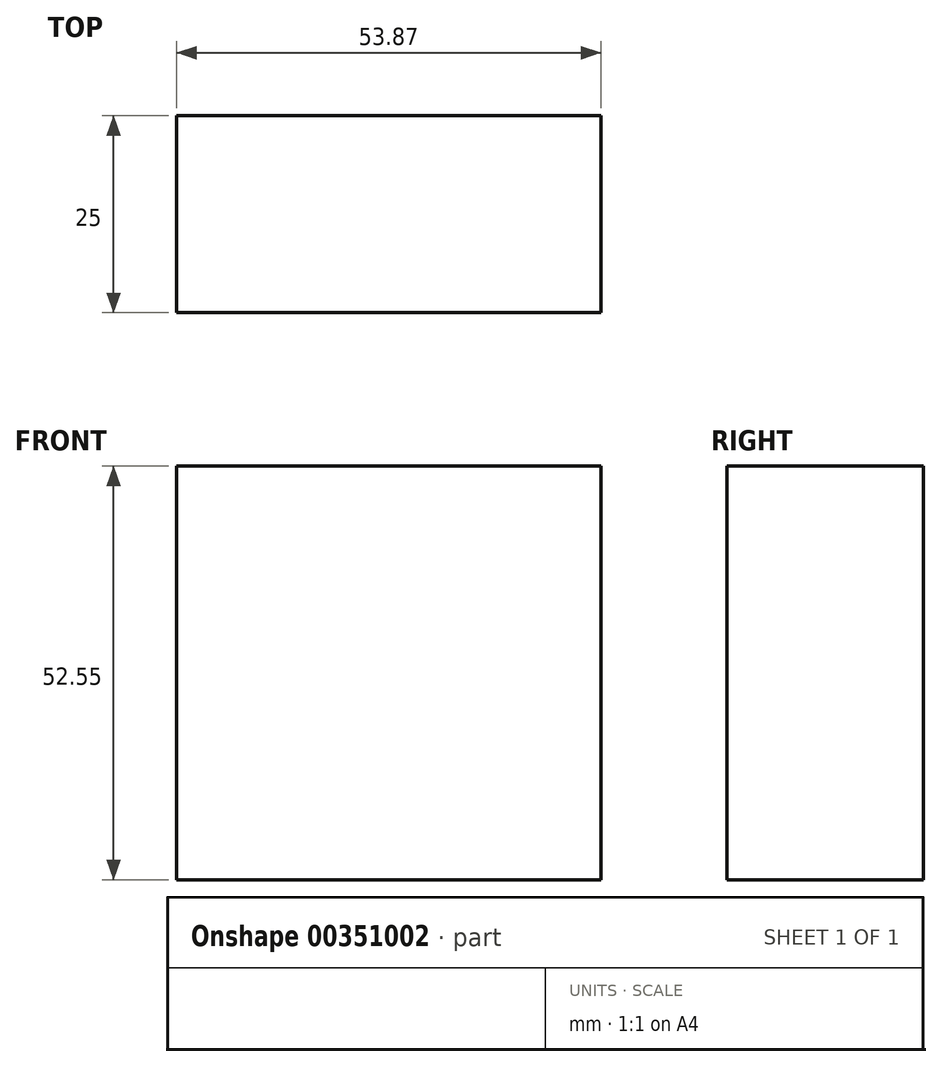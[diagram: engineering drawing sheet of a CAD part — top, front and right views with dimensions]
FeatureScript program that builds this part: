
annotation { "Feature Type Name" : "Feature", "Feature Type Description" : "" }
export const myFeature = defineFeature(function(context is Context, id is Id, definition is map)
    precondition{}
    {
        {
            var Q0;
            Q0=qCreatedBy(makeId("Front.planeOp"),FACE);
            var sketch = newSketch(context, id + "F0", { "sketchPlane" : qUnion([Q0])});
            skLineSegment(sketch, "E0.bottom", {"start": v(-104.18, 12.12) * mm, "end": v(-50.3, 12.12) * mm});
            skLineSegment(sketch, "E0.top", {"start": v(-104.18, 64.67) * mm, "end": v(-50.3, 64.67) * mm});
            skLineSegment(sketch, "E0.left", {"start": v(-104.18, 12.12) * mm, "end": v(-104.18, 64.67) * mm});
            skLineSegment(sketch, "E0.right", {"start": v(-50.3, 12.12) * mm, "end": v(-50.3, 64.67) * mm});
            skPoint(sketch, "E0.middle", {"position": v(-77.24, 38.4) * mm});
            skSolve(sketch);
        }
        {
            var Q0;
            Q0=makeQuery(id+"F0.imprint","IMPRINT",FACE,{"disambiguationData":[TD([[makeQuery(id+"F0.imprint","IMPRINT",EDGE,{"derivedFrom":sQuery(id+"F0.wireOp",EDGE,"E0.bottom")}),1.0]])]});
            extrude(context, id + "F1", {"entities" : qUnion([Q0]), "depth" : 25 * mm});
        }
    });
